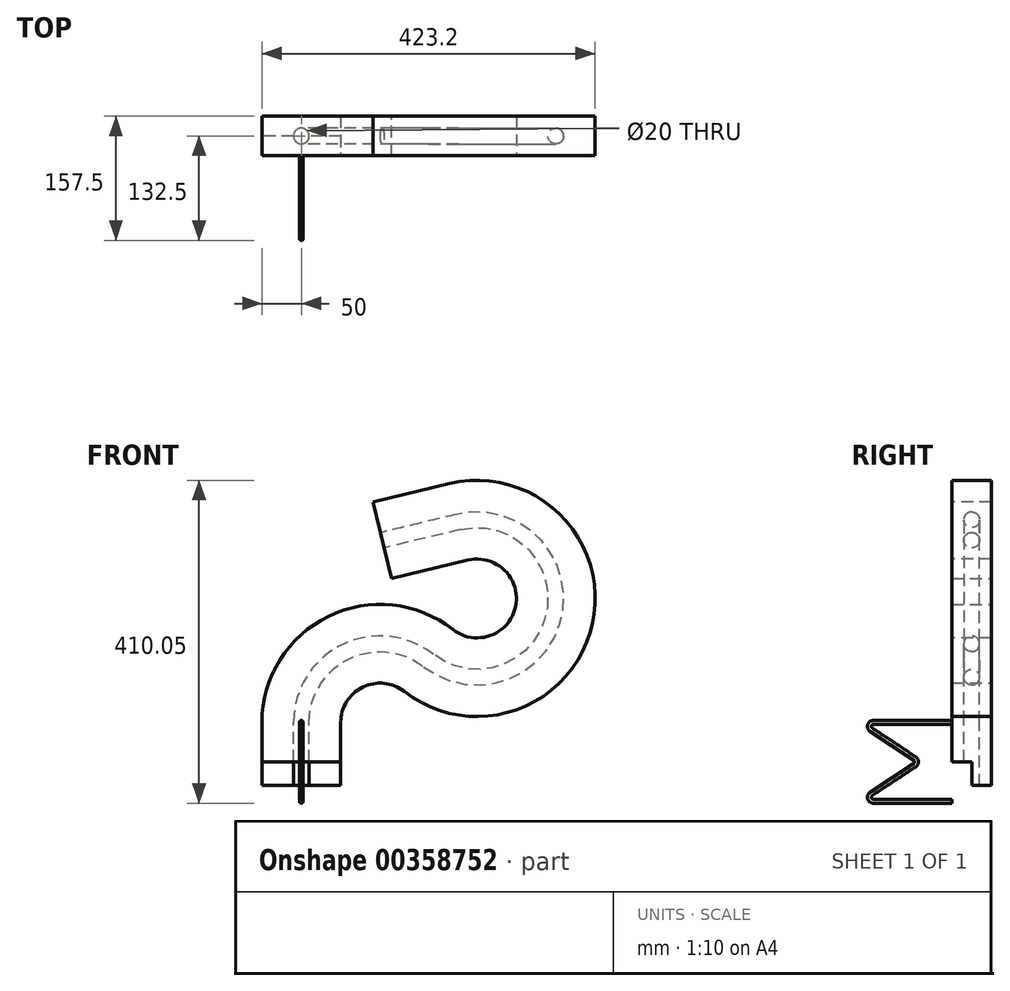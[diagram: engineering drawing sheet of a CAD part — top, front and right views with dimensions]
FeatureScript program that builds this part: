
annotation { "Feature Type Name" : "Feature", "Feature Type Description" : "" }
export const myFeature = defineFeature(function(context is Context, id is Id, definition is map)
    precondition{}
    {
        {
            var Q0;
            Q0=qCreatedBy(makeId("Top.planeOp"),FACE);
            var sketch = newSketch(context, id + "F0", { "sketchPlane" : qUnion([Q0])});
            skLineSegment(sketch, "E0", {"start": v(0, 0) * mm, "end": v(100, 0) * mm});
            skLineSegment(sketch, "E1", {"start": v(100, 0) * mm, "end": v(100, -50) * mm});
            skLineSegment(sketch, "E2", {"start": v(100, -50) * mm, "end": v(0, -50) * mm});
            skLineSegment(sketch, "E3", {"start": v(0, -50) * mm, "end": v(0, 0) * mm});
            skSolve(sketch);
        }
        {
            var Q0;
            Q0=makeQuery(id+"F0.imprint","IMPRINT",FACE,{"disambiguationData":[TD([[makeQuery(id+"F0.imprint","IMPRINT",EDGE,{"derivedFrom":sQuery(id+"F0.wireOp",EDGE,"E0")}),-1.0]])]});
            extrude(context, id + "F1", {"entities" : qUnion([Q0]), "depth" : 30 * mm});
        }
        {
            var Q0;
            Q0=makeQuery(id+"F1.opExtrude","CAP_FACE",FACE,{"disambiguationData":[OSD([sQuery(id+"F0.wireOp",EDGE,"E0"),sQuery(id+"F0.wireOp",EDGE,"E1"),sQuery(id+"F0.wireOp",EDGE,"E2"),sQuery(id+"F0.wireOp",EDGE,"E3")])],"isStart":false});
            var sketch = newSketch(context, id + "F2", { "sketchPlane" : qUnion([Q0])});
            skLineSegment(sketch, "E4", {"start": v(0, 0) * mm, "end": v(50, 0) * mm, "construction": true});
            skLineSegment(sketch, "E5", {"start": v(50, 0) * mm, "end": v(50, -25) * mm, "construction": true});
            skCircle(sketch, "E6", {"center": v(50, -25) * mm, "radius": 10 * mm});
            skSolve(sketch);
        }
        {
            var Q0;
            Q0=makeQuery(id+"F2.imprint","IMPRINT",FACE,{"disambiguationData":[TD([[makeQuery(id+"F2.imprint","IMPRINT",EDGE,{"derivedFrom":sQuery(id+"F2.wireOp",EDGE,"E6")}),1.0]])]});
            extrude(context, id + "F3", {"entities" : qUnion([Q0]), "operationType" : NewBodyOperationType.REMOVE, "oppositeDirection" : true, "depth" : 30 * mm});
        }
        {
            var Q0;
            Q0=makeQuery(id+"F2.imprint","IMPRINT",FACE,{"disambiguationData":[TD([[makeQuery(id+"F2.imprint","IMPRINT",EDGE,{"derivedFrom":sQuery(id+"F2.wireOp",EDGE,"E6")}),-1.0]])]});
            var sketch = newSketch(context, id + "F4", { "sketchPlane" : qUnion([Q0])});
            skLineSegment(sketch, "E7.0.0", {"start": v(0, 0) * mm, "end": v(0, -50) * mm});
            skLineSegment(sketch, "E7.0.1", {"start": v(0, -50) * mm, "end": v(100, -50) * mm});
            skLineSegment(sketch, "E7.0.2", {"start": v(100, -50) * mm, "end": v(100, 0) * mm});
            skLineSegment(sketch, "E7.0.3", {"start": v(100, 0) * mm, "end": v(0, 0) * mm});
            skLineSegment(sketch, "E8", {"start": v(0, -25) * mm, "end": v(100, -25) * mm});
            skSolve(sketch);
        }
        {
            var Q0;
            {var subQ6=sQuery(id+"F4.wireOp",EDGE,"E7.0.1");Q0=makeQuery(id+"F4.imprint","IMPRINT",FACE,{"disambiguationData":[TD([[makeQuery(id+"F4.imprint","IMPRINT",EDGE,{"derivedFrom":subQ6}),-1.0]])]});}
            extrude(context, id + "F5", {"entities" : qUnion([Q0]), "operationType" : NewBodyOperationType.REMOVE, "endBound" : BoundingType.UP_TO_NEXT, "oppositeDirection" : true, "depth" : 25 * mm});
        }
        {
            var Q0;
            {var subQ0=sQuery(id+"F4.wireOp",EDGE,"E8");Q0=makeQuery(id+"F5.boolean.opBoolean","COPY",FACE,{"derivedFrom":makeQuery(id+"F5.opExtrude","SWEPT_FACE",FACE,{"disambiguationData":[OSD([subQ0]),TDD([makeQuery(id+"F4.imprint","IMPRINT",EDGE,{"disambiguationData":[TD([[makeQuery(id+"F4.imprint","INTERSECT",VERTEX,{"derivedFrom":[sQuery(id+"F4.wireOp",EDGE,"E7.0.2"),subQ0]}),1.0]])],"derivedFrom":subQ0})])]})});}
            var sketch = newSketch(context, id + "F6", { "sketchPlane" : qUnion([Q0])});
            skPoint(sketch, "E9.0", {"position": v(50, 30) * mm});
            skPoint(sketch, "E9.1", {"position": v(50, 30) * mm});
            skLineSegment(sketch, "E10", {"start": v(50, 30) * mm, "end": v(50, 80) * mm});
            skArc(sketch, "E11", {"start": v(211.6, 158.77) * mm, "mid": v(106.18, 169.89) * mm, "end": v(50, 80) * mm});
            skArc(sketch, "E12", {"start": v(211.6, 158.77) * mm, "mid": v(370.9, 216.24) * mm, "end": v(250, 334.82) * mm});
            skLineSegment(sketch, "E13", {"start": v(250, 334.82) * mm, "end": v(152.73, 311.61) * mm});
            skPoint(sketch, "E14.orphan", {"position": v(250, 80) * mm});
            skSolve(sketch);
        }
        {
            var Q0;
            Q0=makeQuery(id+"F2.imprint","IMPRINT",FACE,{"disambiguationData":[TD([[makeQuery(id+"F2.imprint","IMPRINT",EDGE,{"derivedFrom":sQuery(id+"F2.wireOp",EDGE,"E6")}),-1.0]])]});
            var Q1;
            Q1=sQuery(id+"F6.wireOp",EDGE,"E10");
            var Q2;
            Q2=sQuery(id+"F6.wireOp",EDGE,"E11");
            var Q3;
            Q3=sQuery(id+"F6.wireOp",EDGE,"E12");
            var Q4;
            Q4=sQuery(id+"F6.wireOp",EDGE,"E13");
            sweep(context, id + "F7", {"operationType" : NewBodyOperationType.ADD, "profiles" : qUnion([Q0]), "path" : qUnion([Q1, Q2, Q3, Q4])});
        }
        {
            var Q0;
            Q0=makeQuery(id+"F7.opSweep","SWEPT_FACE",FACE,{"disambiguationData":[OSD([sQuery(id+"F0.wireOp",EDGE,"E2"),sQuery(id+"F6.wireOp",EDGE,"E10")])]});
            var sketch = newSketch(context, id + "F8", { "sketchPlane" : qUnion([Q0])});
            skLineSegment(sketch, "E15", {"start": v(50, 30) * mm, "end": v(50, 80) * mm, "construction": true});
            skCircle(sketch, "E16", {"center": v(50, 80) * mm, "radius": 2.5 * mm});
            skCircle(sketch, "E17", {"center": v(0, 80) * mm, "radius": 3.33 * mm});
            skSolve(sketch);
        }
        {
            var Q0;
            {var subQ0=sQuery(id+"F0.wireOp",EDGE,"E3");Q0=makeQuery(id+"F7.boolean.opBoolean","MERGE",FACE,{"derivedFrom":[makeQuery(id+"F1.opExtrude","SWEPT_FACE",FACE,{"disambiguationData":[OSD([subQ0])]}),makeQuery(id+"F7.opSweep","SWEPT_FACE",FACE,{"disambiguationData":[OSD([subQ0,sQuery(id+"F6.wireOp",EDGE,"E10")])]})]});}
            cPlane(context, id + "F9", {"entities" : qUnion([Q0]), "cplaneType" : CPlaneType.OFFSET, "offset" : 50 * mm, "oppositeDirection" : true, "width" : 150 * mm, "height" : 150 * mm});
        }
        {
            var Q0;
            Q0=qCreatedBy(id+"F9.planeOp",FACE);
            var sketch = newSketch(context, id + "F10", { "sketchPlane" : qUnion([Q0])});
            skPoint(sketch, "E18.0", {"position": v(50, 80) * mm});
            skLineSegment(sketch, "E19", {"start": v(50, 80) * mm, "end": v(150, 80) * mm});
            skPoint(sketch, "E20.0", {"position": v(50, 30) * mm});
            skLineSegment(sketch, "E21", {"start": v(50, 30) * mm, "end": v(100, 30) * mm, "construction": true});
            skLineSegment(sketch, "E22", {"start": v(100, 30) * mm, "end": v(100, 35) * mm, "construction": true});
            skArc(sketch, "E23", {"start": v(152.76, 70.83) * mm, "mid": v(154.79, 76.44) * mm, "end": v(150, 80) * mm});
            skArc(sketch, "E24", {"start": v(97.24, 34.17) * mm, "mid": v(95.6, 32.37) * mm, "end": v(95, 30) * mm});
            skLineSegment(sketch, "E25", {"start": v(152.76, 70.83) * mm, "end": v(97.24, 34.17) * mm});
            skSolve(sketch);
        }
        {
            var Q0;
            Q0=makeQuery(id+"F8.imprint","IMPRINT",FACE,{"disambiguationData":[TD([[makeQuery(id+"F8.imprint","IMPRINT",EDGE,{"derivedFrom":sQuery(id+"F8.wireOp",EDGE,"E16")}),1.0]])]});
            var Q1;
            Q1=sQuery(id+"F10.wireOp",EDGE,"E19");
            var Q2;
            Q2=sQuery(id+"F10.wireOp",EDGE,"E23");
            var Q3;
            Q3=sQuery(id+"F10.wireOp",EDGE,"E25");
            var Q4;
            Q4=sQuery(id+"F10.wireOp",EDGE,"E24");
            sweep(context, id + "F11", {"profiles" : qUnion([Q0]), "path" : qUnion([Q1, Q2, Q3, Q4])});
        }
        {
            var Q0;
            Q0=makeQuery(id+"F11.opSweep","SWEPT_BODY",BODY,{"disambiguationData":[OSD([sQuery(id+"F8.wireOp",EDGE,"E16"),sQuery(id+"F10.wireOp",EDGE,"E24")])]});
            var Q1;
            Q1=makeQuery(id+"F11.opSweep","CAP_FACE",FACE,{"disambiguationData":[OSD([sQuery(id+"F8.wireOp",EDGE,"E16"),sQuery(id+"F10.wireOp",VERTEX,"E24.end")])],"isStart":false});
            mirror(context, id + "F12", {"operationType" : NewBodyOperationType.ADD, "entities" : qUnion([Q0]), "mirrorPlane" : qUnion([Q1])});
        }
    });
